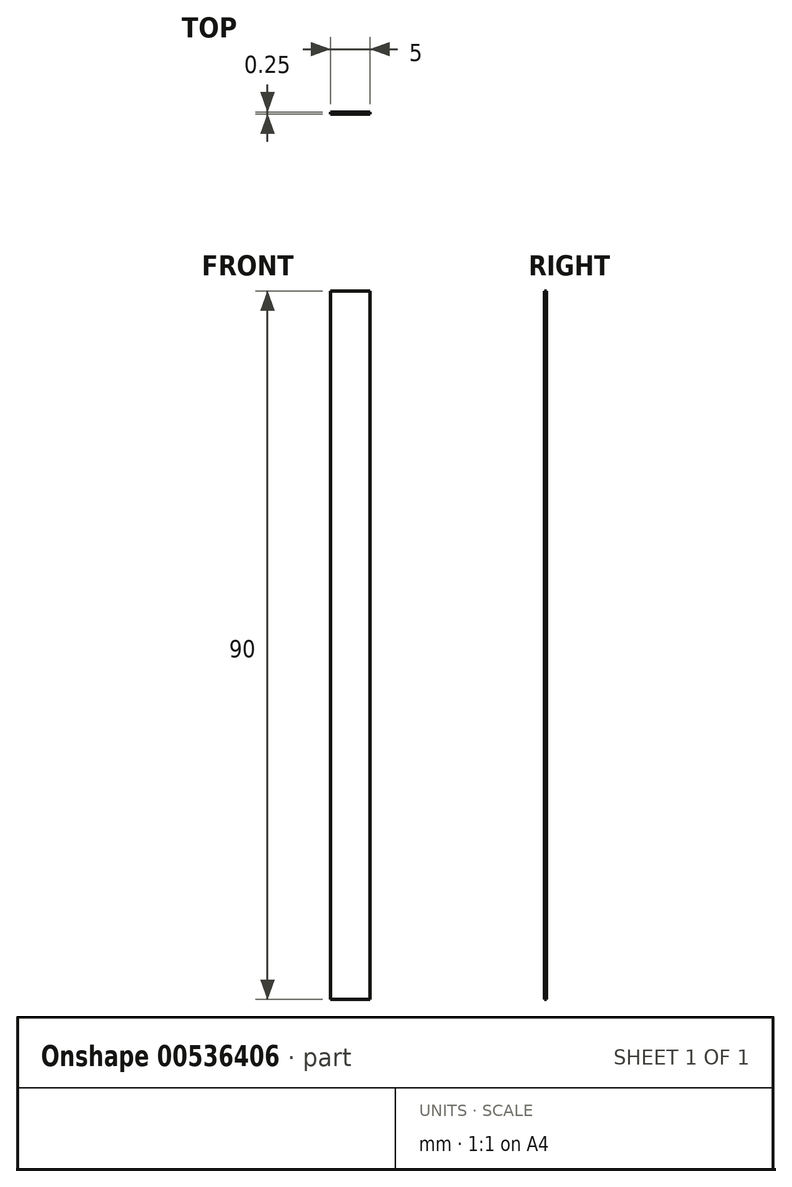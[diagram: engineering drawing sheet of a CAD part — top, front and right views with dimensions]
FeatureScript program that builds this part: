
annotation { "Feature Type Name" : "Feature", "Feature Type Description" : "" }
export const myFeature = defineFeature(function(context is Context, id is Id, definition is map)
    precondition{}
    {
        {
            var Q0;
            Q0=qCreatedBy(makeId("Front.planeOp"),FACE);
            var sketch = newSketch(context, id + "F0", { "sketchPlane" : qUnion([Q0])});
            skLineSegment(sketch, "E0.bottom", {"start": v(2.5, -45) * mm, "end": v(-2.5, -45) * mm});
            skLineSegment(sketch, "E0.top", {"start": v(2.5, 45) * mm, "end": v(-2.5, 45) * mm});
            skLineSegment(sketch, "E0.left", {"start": v(2.5, -45) * mm, "end": v(2.5, 45) * mm});
            skLineSegment(sketch, "E0.right", {"start": v(-2.5, -45) * mm, "end": v(-2.5, 45) * mm});
            skPoint(sketch, "E0.middle", {"position": v(0, 0) * mm});
            skSolve(sketch);
        }
        {
            var Q0;
            Q0=makeQuery(id+"F0.imprint","IMPRINT",FACE,{"disambiguationData":[TD([[makeQuery(id+"F0.imprint","IMPRINT",EDGE,{"derivedFrom":sQuery(id+"F0.wireOp",EDGE,"E0.bottom")}),-1.0]])]});
            extrude(context, id + "F1", {"entities" : qUnion([Q0]), "depth" : 0.25 * mm});
        }
    });
